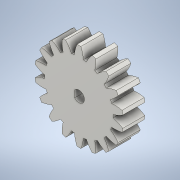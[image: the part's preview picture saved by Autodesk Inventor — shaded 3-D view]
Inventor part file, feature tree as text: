
AUTODESK INVENTOR PART (.ipt)
format: ipt  version: 2022.2 (Build 262287010, 287A)  size: 260,608 bytes
history: native  units: mm (DEFAULTED — no unit token found)
features: sketch x4, extrude x3, plane x3, other x3
ambient origin geometry x8: Origin, YZ Plane, XZ Plane, XY Plane, X Axis, Y Axis, Z Axis, Center Point
bodies: Solid1 (feature_tree)
feature tree (13):
  extrude  "Extrusion1"  Depth=10.0mm TaperAngle=0.0deg
  plane  "Work Plane2"
  plane  "Work Plane8"
  plane  "Work Plane9"
  other  "Engranaje recto"
  extrude  "Extrusión2"  Depth=10.0mm TaperAngle=0.0deg
  extrude  "Extrusión4"  Depth=1.745329mm TaperAngle=0.0deg
  sketch  "Sketch1"  dims[d0=40.0mm d1=10.0mm d2=0.0mm]
  sketch  "Sketch2"  dims[d3=36.0mm d4=10.0mm d5=0.0mm]
  other  "Srf1"
  sketch  "Boceto3"  dims[d16=90.0mm d17=0.0mm d34=1.745329mm]
  sketch  "Boceto6"  dims[d39=0.0mm d41=0.0mm d43=90.0mm d46=90.0mm d47=0.0mm d48=0.0mm d49=5.0mm d50=0.0mm d51=0.0mm d56=10.0mm d57=0.0mm]
  other  "Diámetro de separación"
